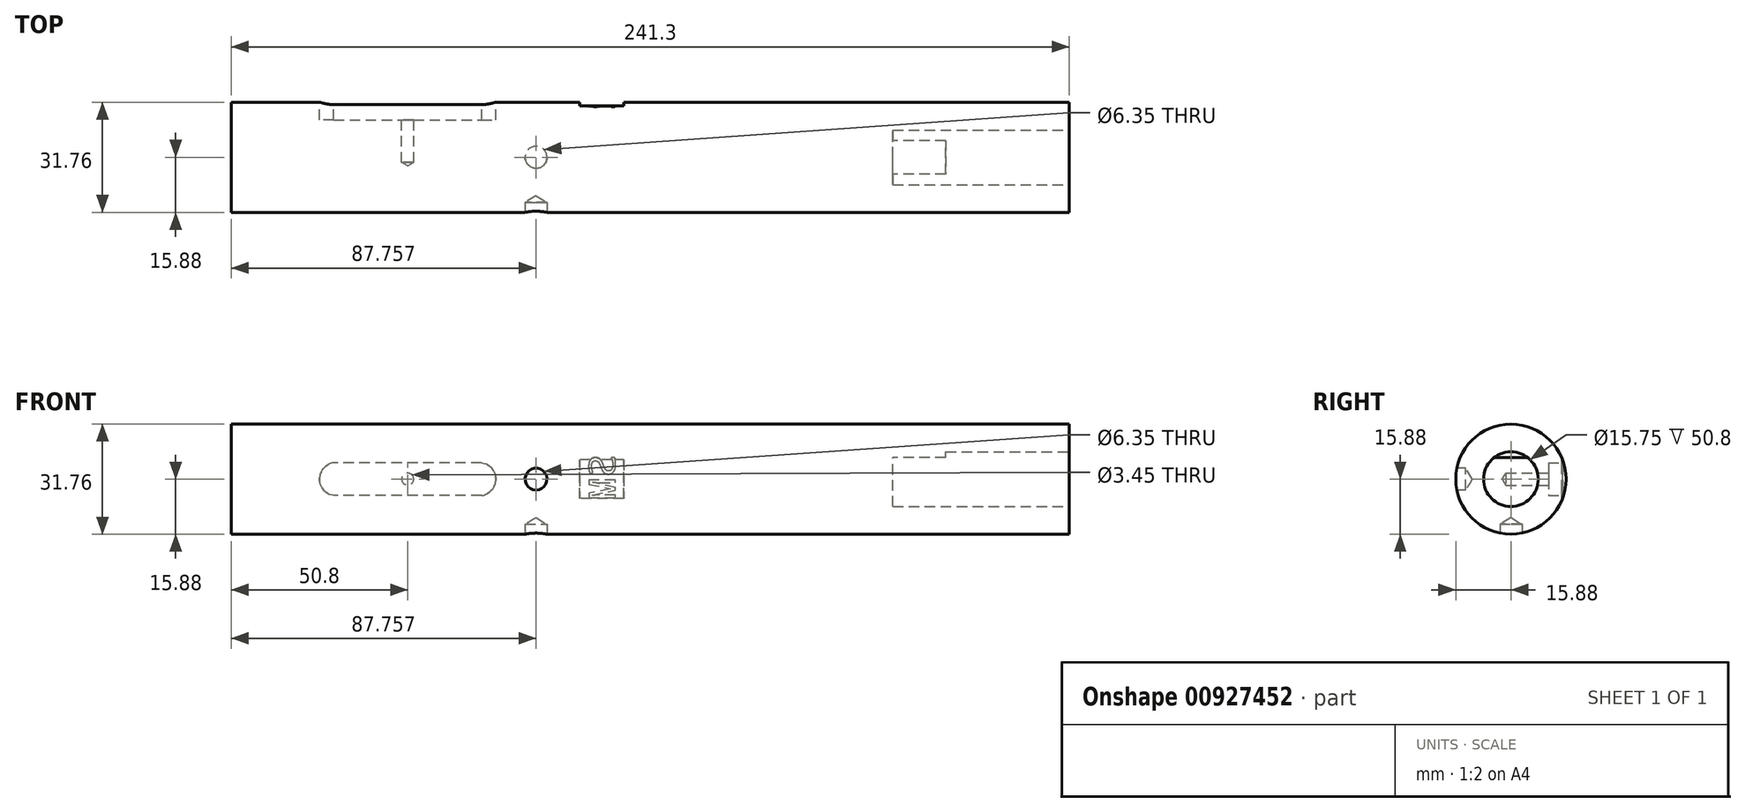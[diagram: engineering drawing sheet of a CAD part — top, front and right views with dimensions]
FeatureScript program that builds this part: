
annotation { "Feature Type Name" : "Feature", "Feature Type Description" : "" }
export const myFeature = defineFeature(function(context is Context, id is Id, definition is map)
    precondition{}
    {
        {
            var Q0;
            Q0=qCreatedBy(makeId("Right.planeOp"),FACE);
            var sketch = newSketch(context, id + "F0", { "sketchPlane" : qUnion([Q0])});
            skCircle(sketch, "E0", {"center": v(0, 0) * mm, "radius": 15.88 * mm});
            skSolve(sketch);
        }
        {
            var Q0;
            Q0 = qSketchRegion(id + "F0", true);
            extrude(context, id + "F1", {"entities" : qUnion([Q0]), "depth" : 241.3 * mm, "offsetDistance" : 25.4 * mm});
        }
        {
            var Q0;
            Q0=qCreatedBy(makeId("Front.planeOp"),FACE);
            cPlane(context, id + "F2", {"entities" : qUnion([Q0]), "cplaneType" : CPlaneType.OFFSET, "offset" : 15.88 * mm, "oppositeDirection" : true, "width" : 152.4 * mm, "height" : 152.4 * mm});
        }
        {
            var Q0;
            Q0=qCreatedBy(id+"F2.planeOp",FACE);
            var sketch = newSketch(context, id + "F3", { "sketchPlane" : qUnion([Q0])});
            skLineSegment(sketch, "E1.bottom", {"start": v(29.52, 4.74) * mm, "end": v(72.08, 4.74) * mm});
            skLineSegment(sketch, "E1.top", {"start": v(29.52, -4.74) * mm, "end": v(72.08, -4.74) * mm});
            skPoint(sketch, "E1.middle", {"position": v(50.8, 0) * mm});
            skArc(sketch, "E2", {"start": v(29.52, 4.74) * mm, "mid": v(25.4, 0) * mm, "end": v(29.52, -4.74) * mm});
            skArc(sketch, "E3", {"start": v(72.08, -4.74) * mm, "mid": v(76.2, 0) * mm, "end": v(72.08, 4.74) * mm});
            skSolve(sketch);
        }
        {
            var Q0;
            Q0=makeQuery(id+"F3.imprint","IMPRINT",FACE,{"disambiguationData":[TD([[makeQuery(id+"F3.imprint","IMPRINT",EDGE,{"derivedFrom":sQuery(id+"F3.wireOp",EDGE,"E1.bottom")}),-1.0]])]});
            extrude(context, id + "F4", {"entities" : qUnion([Q0]), "operationType" : NewBodyOperationType.REMOVE, "depth" : 5.08 * mm, "offsetDistance" : 25.4 * mm});
        }
        {
            var Q0;
            Q0=makeQuery(id+"F4.boolean.opBoolean","COPY",FACE,{"derivedFrom":makeQuery(id+"F4.opExtrude","CAP_FACE",FACE,{"disambiguationData":[OSD([sQuery(id+"F3.wireOp",EDGE,"E1.bottom"),sQuery(id+"F3.wireOp",EDGE,"E1.top"),sQuery(id+"F3.wireOp",EDGE,"E2"),sQuery(id+"F3.wireOp",EDGE,"E3")])],"isStart":false})});
            var sketch = newSketch(context, id + "F5", { "sketchPlane" : qUnion([Q0])});
            skCircle(sketch, "E4", {"center": v(-50.8, 0) * mm, "radius": 2.41 * mm});
            skSolve(sketch);
        }
        {
            var Q0;
            Q0=qCreatedBy(makeId("Top.planeOp"),FACE);
            cPlane(context, id + "F6", {"entities" : qUnion([Q0]), "cplaneType" : CPlaneType.OFFSET, "offset" : 15.88 * mm, "oppositeDirection" : true, "width" : 152.4 * mm, "height" : 152.4 * mm});
        }
        {
            var Q0;
            Q0=qCreatedBy(id+"F6.planeOp",FACE);
            var sketch = newSketch(context, id + "F7", { "sketchPlane" : qUnion([Q0])});
            skCircle(sketch, "E5", {"center": v(87.76, 0) * mm, "radius": 3.18 * mm});
            skSolve(sketch);
        }
        {
            var Q0;
            Q0=makeQuery(id+"F1.opExtrude","CAP_FACE",FACE,{"disambiguationData":[OSD([sQuery(id+"F0.wireOp",EDGE,"E0")])],"isStart":false});
            var sketch = newSketch(context, id + "F8", { "sketchPlane" : qUnion([Q0])});
            skLineSegment(sketch, "E6", {"start": v(0, -15.88) * mm, "end": v(-15.88, 0) * mm, "construction": true});
            skSolve(sketch);
        }
        {
            var Q0;
            Q0=sQuery(id+"F8.wireOp",EDGE,"E6");
            cPlane(context, id + "F9", {"entities" : qUnion([Q0]), "cplaneType" : CPlaneType.LINE_ANGLE, "offset" : 25.4 * mm, "angle" : 0 * degree, "width" : 152.4 * mm, "height" : 152.4 * mm});
        }
        {
            var Q0;
            Q0=makeQuery(id+"F8.imprint","IMPRINT",FACE,{"disambiguationData":[TD([[makeQuery(id+"F8.imprint","IMPRINT",EDGE,{"derivedFrom":makeQuery(id+"F1.opExtrude","CAP_EDGE",EDGE,{"disambiguationData":[OSD([sQuery(id+"F0.wireOp",EDGE,"E0")])],"isStart":false})}),1.0]])]});
            var sketch = newSketch(context, id + "F10", { "sketchPlane" : qUnion([Q0])});
            skCircle(sketch, "E7", {"center": v(0, 0) * mm, "radius": 7.87 * mm});
            skSolve(sketch);
        }
        {
            var Q0;
            Q0 = qSketchRegion(id + "F10", true);
            extrude(context, id + "F11", {"entities" : qUnion([Q0]), "operationType" : NewBodyOperationType.REMOVE, "oppositeDirection" : true, "depth" : 50.8 * mm, "offsetDistance" : 25.4 * mm});
        }
        {
            var Q0;
            Q0=qCreatedBy(id+"F2.planeOp",FACE);
            var sketch = newSketch(context, id + "F12", { "sketchPlane" : qUnion([Q0])});
            skLineSegment(sketch, "E8.bottom", {"start": v(112.97, -12.89) * mm, "end": v(100.27, -12.89) * mm});
            skLineSegment(sketch, "E8.top", {"start": v(112.97, 12.89) * mm, "end": v(100.27, 12.89) * mm});
            skLineSegment(sketch, "E8.left", {"start": v(112.97, -12.89) * mm, "end": v(112.97, 12.89) * mm});
            skLineSegment(sketch, "E8.right", {"start": v(100.27, -12.89) * mm, "end": v(100.27, 12.89) * mm});
            skPoint(sketch, "E8.middle", {"position": v(106.62, 0) * mm});
            skSolve(sketch);
        }
        {
            var Q0;
            Q0 = qSketchRegion(id + "F12", true);
            extrude(context, id + "F13", {"entities" : qUnion([Q0]), "operationType" : NewBodyOperationType.REMOVE, "depth" : 1.02 * mm, "offsetDistance" : 25.4 * mm});
        }
        {
            var Q0;
            Q0=makeQuery(id+"F13.boolean.opBoolean","COPY",FACE,{"derivedFrom":makeQuery(id+"F13.opExtrude","CAP_FACE",FACE,{"disambiguationData":[OSD([sQuery(id+"F12.wireOp",EDGE,"E8.bottom"),sQuery(id+"F12.wireOp",EDGE,"E8.top"),sQuery(id+"F12.wireOp",EDGE,"E8.left"),sQuery(id+"F12.wireOp",EDGE,"E8.right")])],"isStart":false})});
            var sketch = newSketch(context, id + "F14", { "sketchPlane" : qUnion([Q0])});
            skText(sketch, "E9", { "text": "M", "fontName": "DroidSansMono.ttf"});
            skText(sketch, "E10", { "text": "S", "fontName": "DroidSansMono.ttf"});
            const initialGuessF14  = {"E9": [-0.11057, 0.00038, 0, -1, 0.00762], "E10": [-0.11057, 0.00706, 0, -1, 0.00762]};
            skSetInitialGuess(sketch, initialGuessF14);
            skSolve(sketch);
        }
        {
            var Q0;
            Q0 = qSketchRegion(id + "F14", true);
            extrude(context, id + "F15", {"entities" : qUnion([Q0]), "operationType" : NewBodyOperationType.REMOVE, "oppositeDirection" : true, "depth" : 0.25 * mm, "offsetDistance" : 25.4 * mm});
        }
        {
            var Q0;
            Q0=qCreatedBy(makeId("Front.planeOp"),FACE);
            cPlane(context, id + "F16", {"entities" : qUnion([Q0]), "cplaneType" : CPlaneType.OFFSET, "offset" : 15.88 * mm, "width" : 152.4 * mm, "height" : 152.4 * mm});
        }
        {
            var Q0;
            Q0=qCreatedBy(id+"F16.planeOp",FACE);
            var sketch = newSketch(context, id + "F17", { "sketchPlane" : qUnion([Q0])});
            skCircle(sketch, "E11", {"center": v(87.76, 0) * mm, "radius": 3.18 * mm});
            skSolve(sketch);
        }
        {
            var Q0;
            Q0=makeQuery(id+"F8.imprint","IMPRINT",FACE,{"disambiguationData":[TD([[makeQuery(id+"F8.imprint","IMPRINT",EDGE,{"derivedFrom":makeQuery(id+"F1.opExtrude","CAP_EDGE",EDGE,{"disambiguationData":[OSD([sQuery(id+"F0.wireOp",EDGE,"E0")])],"isStart":false})}),1.0]])]});
            cPlane(context, id + "F18", {"entities" : qUnion([Q0]), "cplaneType" : CPlaneType.OFFSET, "offset" : 50.8 * mm, "oppositeDirection" : true, "width" : 152.4 * mm, "height" : 152.4 * mm});
        }
        {
            var Q0;
            Q0=qCreatedBy(id+"F18.planeOp",FACE);
            var sketch = newSketch(context, id + "F19", { "sketchPlane" : qUnion([Q0])});
            skLineSegment(sketch, "E12", {"start": v(-4.83, 6.22) * mm, "end": v(4.83, 6.22) * mm});
            skArc(sketch, "E13", {"start": v(4.83, 6.22) * mm, "mid": v(0, 7.87) * mm, "end": v(-4.83, 6.22) * mm});
            skSolve(sketch);
        }
        {
            var Q0;
            Q0 = qSketchRegion(id + "F19", true);
            extrude(context, id + "F20", {"entities" : qUnion([Q0]), "operationType" : NewBodyOperationType.ADD, "depth" : 15.24 * mm, "offsetDistance" : 25.4 * mm});
        }
        {
            var Q0;
            Q0=sQuery(id+"F7.wireOp",VERTEX,"E5.center");
            var Q1;
            Q1=makeQuery(id+"F1.opExtrude","SWEPT_BODY",BODY,{"disambiguationData":[OSD([sQuery(id+"F0.wireOp",EDGE,"E0")])]});
            hole(context, id + "F21", {"style" : HoleStyle.SIMPLE, "endStyle" : HoleEndStyle.BLIND, "oppositeDirection" : true, "holeDiameter" : 6.35 * mm, "majorDiameter" : 6.35 * mm, "holeDepth" : 2.54 * mm, "isTappedThrough" : true, "tappedDepth" : 2.54 * mm, "tapClearance" : 5, "locations" : qUnion([Q0]), "scope" : qUnion([Q1])});
        }
        {
            var Q0;
            Q0=sQuery(id+"F17.wireOp",VERTEX,"E11.center");
            var Q1;
            Q1=makeQuery(id+"F1.opExtrude","SWEPT_BODY",BODY,{"disambiguationData":[OSD([sQuery(id+"F0.wireOp",EDGE,"E0")])]});
            hole(context, id + "F22", {"style" : HoleStyle.SIMPLE, "endStyle" : HoleEndStyle.BLIND, "holeDiameter" : 6.35 * mm, "majorDiameter" : 6.35 * mm, "holeDepth" : 2.54 * mm, "isTappedThrough" : true, "tappedDepth" : 2.54 * mm, "tapClearance" : 5, "locations" : qUnion([Q0]), "scope" : qUnion([Q1])});
        }
        {
            var Q0;
            Q0=sQuery(id+"F5.wireOp",VERTEX,"E4.center");
            var Q1;
            Q1=makeQuery(id+"F1.opExtrude","SWEPT_BODY",BODY,{"disambiguationData":[OSD([sQuery(id+"F0.wireOp",EDGE,"E0")])]});
            hole(context, id + "F23", {"style" : HoleStyle.SIMPLE, "endStyle" : HoleEndStyle.BLIND, "standardTappedOrClearance" : lookupTablePath({ "standard" : "ANSI", "engagement" : "75%", "pitch" : "36 tpi", "size" : "#8", "type" : "Tapped" }), "standardBlindInLast" : lookupTablePath({ "standard" : "ANSI", "fit" : "Free", "engagement" : "75%", "pitch" : "36 tpi", "size" : "#8", "type" : "Clearance & tapped" }), "holeDiameter" : 3.45 * mm, "majorDiameter" : 4.17 * mm, "showTappedDepth" : true, "holeDepth" : 12.26 * mm, "isTappedThrough" : true, "tappedDepth" : 8.73 * mm, "tapClearance" : 5, "locations" : qUnion([Q0]), "scope" : qUnion([Q1])});
        }
    });
